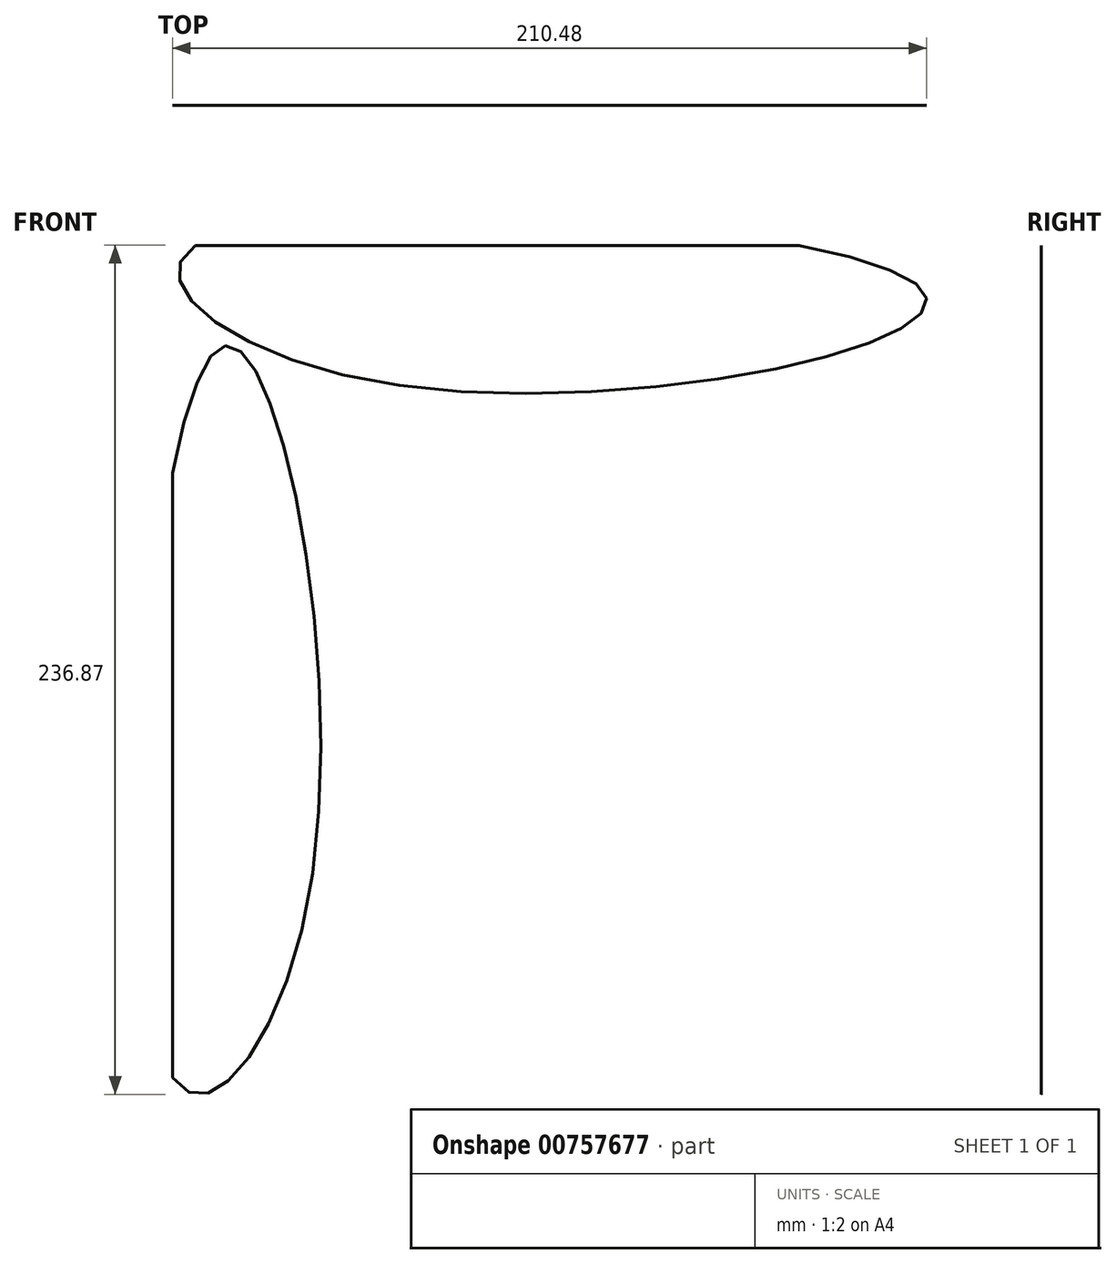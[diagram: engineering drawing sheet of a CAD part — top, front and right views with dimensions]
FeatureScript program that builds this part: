
annotation { "Feature Type Name" : "Feature", "Feature Type Description" : "" }
export const myFeature = defineFeature(function(context is Context, id is Id, definition is map)
    precondition{}
    {
        {
            var Q0;
            Q0=qCreatedBy(makeId("Front.planeOp"),FACE);
            var sketch = newSketch(context, id + "F0", { "sketchPlane" : qUnion([Q0])});
            skLineSegment(sketch, "E0.bottom", {"start": v(152.4, -152.4) * mm, "end": v(-152.4, -152.4) * mm});
            skLineSegment(sketch, "E0.top", {"start": v(152.4, 152.4) * mm, "end": v(-152.4, 152.4) * mm});
            skLineSegment(sketch, "E0.left", {"start": v(152.4, -152.4) * mm, "end": v(152.4, 152.4) * mm});
            skLineSegment(sketch, "E0.right", {"start": v(-152.4, -152.4) * mm, "end": v(-152.4, 152.4) * mm});
            skPoint(sketch, "E0.middle", {"position": v(0, 0) * mm});
            skLineSegment(sketch, "E1", {"start": v(152.4, 152.4) * mm, "end": v(88.9, 152.4) * mm});
            skLineSegment(sketch, "E2", {"start": v(152.4, 152.4) * mm, "end": v(152.4, -16.15) * mm});
            skFitSpline(sketch, "E3", {"points": [v(-145.85, 152.12) * mm, v(-95.05, 114.02) * mm, v(57.35, 139.42) * mm, v(-145.85, 152.12) * mm]});
            skLineSegment(sketch, "E4", {"start": v(-145.85, 152.12) * mm, "end": v(22.7, 152.12) * mm});
            skFitSpline(sketch, "E5", {"points": [v(-152.18, -80.05) * mm, v(-114.08, -29.25) * mm, v(-139.48, 123.15) * mm, v(-152.18, -80.05) * mm]});
            skLineSegment(sketch, "E6", {"start": v(-152.18, -80.05) * mm, "end": v(-152.18, 88.51) * mm});
            skLineSegment(sketch, "E7", {"start": v(152.4, -16.15) * mm, "end": v(88.9, -16.15) * mm});
            skLineSegment(sketch, "E8", {"start": v(88.9, 152.4) * mm, "end": v(88.9, -16.15) * mm});
            skSolve(sketch);
        }
        {
            var Q0;
            {var subQ0=sQuery(id+"F0.wireOp",EDGE,"YxxIDnG9-2LGv-h4ci-ldGZ-wJmBUpsUtbOV");Q0=makeQuery(id+"F0.imprint","IMPRINT",FACE,{"disambiguationData":[TD([[makeQuery(id+"F0.imprint","IMPRINT",EDGE,{"derivedFrom":subQ0}),-1.0]])]});}
            var Q1;
            {var subQ0=sQuery(id+"F0.wireOp",EDGE,"072d48ca-9dcf-435d-b208-5913de50d424");Q1=makeQuery(id+"F0.imprint","IMPRINT",FACE,{"disambiguationData":[TD([[makeQuery(id+"F0.imprint","IMPRINT",EDGE,{"derivedFrom":subQ0}),1.0]])]});}
            var Q2;
            Q2=makeQuery(id+"F0.imprint","IMPRINT",FACE,{"disambiguationData":[TD([[makeQuery(id+"F0.imprint","IMPRINT",EDGE,{"derivedFrom":sQuery(id+"F0.wireOp",EDGE,"a200fde8-d33f-4d68-98c5-69f9329465d8")}),1.0]])]});
            var Q3;
            Q3=makeQuery(id+"F0.imprint","IMPRINT",FACE,{"disambiguationData":[TD([[makeQuery(id+"F0.imprint","IMPRINT",EDGE,{"derivedFrom":sQuery(id+"F0.wireOp",EDGE,"ba52c90b-774d-4c85-81ff-49fb3ef5efc1")}),1.0]])]});
            var Q4;
            {var subQ0=sQuery(id+"F0.wireOp",EDGE,"E1");Q4=makeQuery(id+"F0.imprint","IMPRINT",FACE,{"disambiguationData":[TD([[makeQuery(id+"F0.imprint","IMPRINT",EDGE,{"derivedFrom":subQ0}),1.0]])]});}
            var Q5;
            {var subQ0=sQuery(id+"F0.wireOp",EDGE,"D5TGTZH8-w98d-X97L-FOtW-uaTei0dpTIAP");Q5=makeQuery(id+"F0.imprint","IMPRINT",FACE,{"disambiguationData":[TD([[makeQuery(id+"F0.imprint","IMPRINT",EDGE,{"derivedFrom":subQ0}),-1.0]])]});}
            var Q6;
            Q6=makeQuery(id+"F0.imprint","IMPRINT",FACE,{"disambiguationData":[TD([[makeQuery(id+"F0.imprint","IMPRINT",EDGE,{"derivedFrom":sQuery(id+"F0.wireOp",EDGE,"0pPElIAd-eFF9-AYoV-LtaF-HjRUm90kOVqM")}),-1.0]])]});
            var Q7;
            {var subQ5=sQuery(id+"F0.wireOp",EDGE,"f4acLpoL-qZY5-cZHq-iqsA-Bw3v6SchqLtM");Q7=makeQuery(id+"F0.imprint","IMPRINT",FACE,{"disambiguationData":[TD([[makeQuery(id+"F0.imprint","IMPRINT",EDGE,{"derivedFrom":subQ5}),-1.0]])]});}
            var Q8;
            {var subQ0=sQuery(id+"F0.wireOp",EDGE,"E4");Q8=makeQuery(id+"F0.imprint","IMPRINT",FACE,{"disambiguationData":[TD([[makeQuery(id+"F0.imprint","IMPRINT",EDGE,{"derivedFrom":subQ0}),-1.0]])]});}
            var Q9;
            {var subQ0=sQuery(id+"F0.wireOp",EDGE,"E6");Q9=makeQuery(id+"F0.imprint","IMPRINT",FACE,{"disambiguationData":[TD([[makeQuery(id+"F0.imprint","IMPRINT",EDGE,{"derivedFrom":subQ0}),-1.0]])]});}
            extrude(context, id + "F1", {"entities" : qUnion([Q0, Q1, Q2, Q3, Q4, Q5, Q6, Q7, Q8, Q9]), "depth" : 1 / 203.2 * mm, "offsetDistance" : 25.4 * mm});
        }
    });
